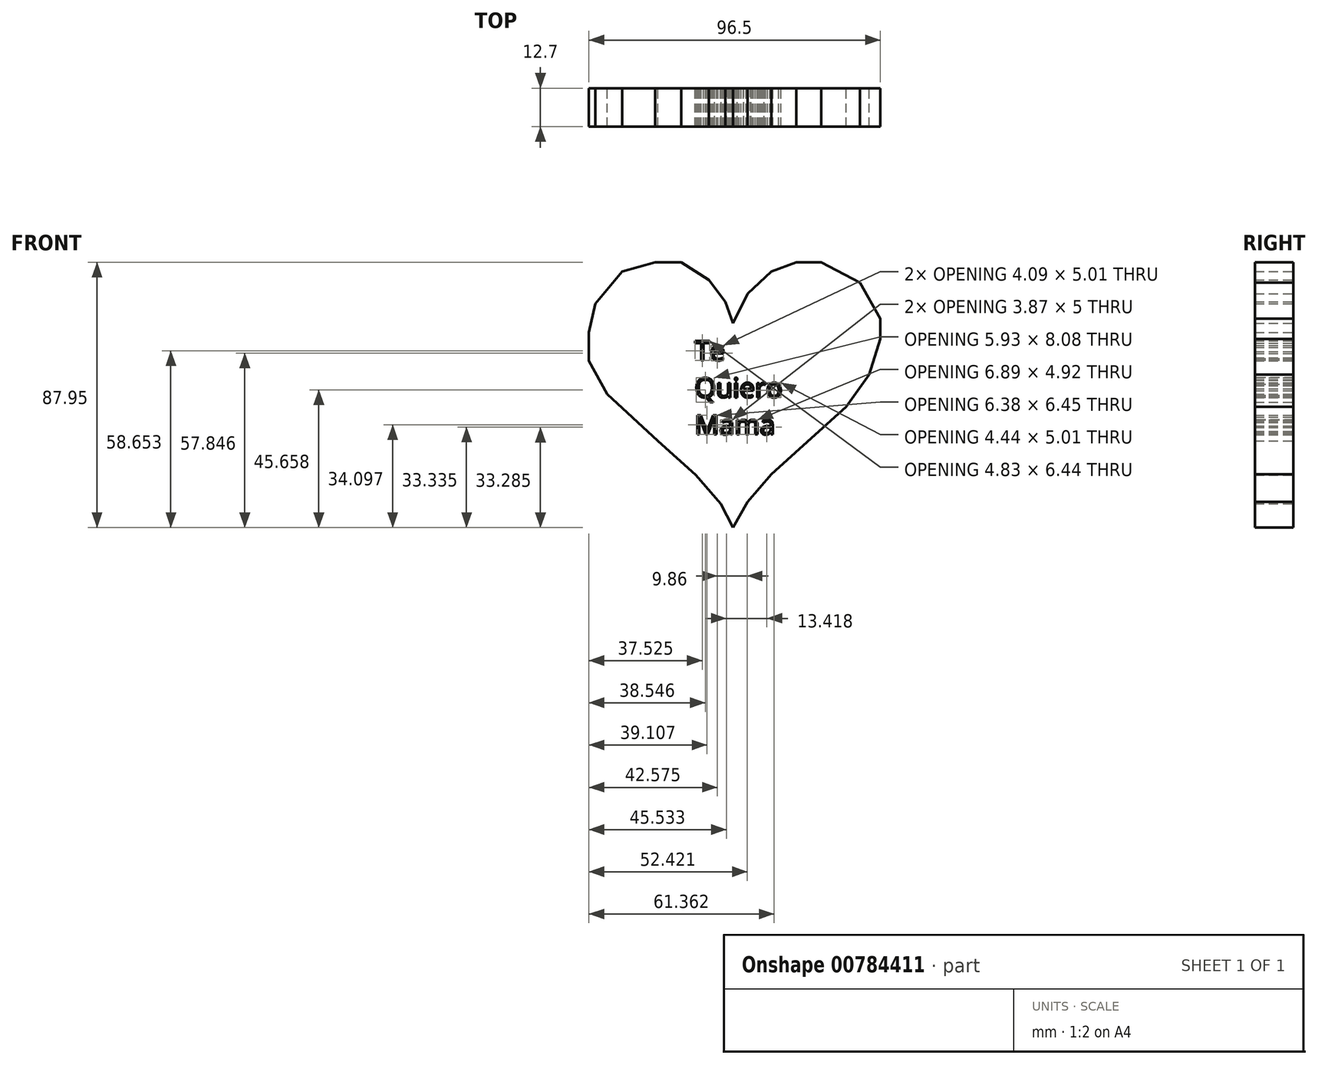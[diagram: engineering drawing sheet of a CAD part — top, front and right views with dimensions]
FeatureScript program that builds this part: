
annotation { "Feature Type Name" : "Feature", "Feature Type Description" : "" }
export const myFeature = defineFeature(function(context is Context, id is Id, definition is map)
    precondition{}
    {
        {
            var Q0;
            Q0=qCreatedBy(makeId("Front.planeOp"),FACE);
            var sketch = newSketch(context, id + "F0", { "sketchPlane" : qUnion([Q0])});
            skLineSegment(sketch, "E0", {"start": v(0, 20.3) * mm, "end": v(4.73, 30.08) * mm});
            skLineSegment(sketch, "E1", {"start": v(4.73, 30.08) * mm, "end": v(12.67, 37.4) * mm});
            skLineSegment(sketch, "E2", {"start": v(12.67, 37.4) * mm, "end": v(20.92, 40.46) * mm});
            skLineSegment(sketch, "E3", {"start": v(20.92, 40.46) * mm, "end": v(29.16, 40.46) * mm});
            skLineSegment(sketch, "E4", {"start": v(29.16, 40.46) * mm, "end": v(41.99, 33.74) * mm});
            skLineSegment(sketch, "E5", {"start": v(41.99, 33.74) * mm, "end": v(48.7, 21.83) * mm});
            skLineSegment(sketch, "E6", {"start": v(48.7, 21.83) * mm, "end": v(48.7, 15.12) * mm});
            skLineSegment(sketch, "E7", {"start": v(48.7, 15.12) * mm, "end": v(45.04, 3.2) * mm});
            skLineSegment(sketch, "E8", {"start": v(45.04, 3.2) * mm, "end": v(37.4, -7.48) * mm});
            skLineSegment(sketch, "E9", {"start": v(37.4, -7.48) * mm, "end": v(25.8, -17.86) * mm});
            skLineSegment(sketch, "E10", {"start": v(25.8, -17.86) * mm, "end": v(12.67, -29.77) * mm});
            skLineSegment(sketch, "E11", {"start": v(12.67, -29.77) * mm, "end": v(4.73, -38.94) * mm});
            skLineSegment(sketch, "E12", {"start": v(4.73, -38.94) * mm, "end": v(0, -47.49) * mm});
            skLineSegment(sketch, "E13", {"start": v(0, -47.49) * mm, "end": v(-4.12, -39.55) * mm});
            skLineSegment(sketch, "E14", {"start": v(-4.12, -39.55) * mm, "end": v(-12.37, -30.08) * mm});
            skLineSegment(sketch, "E15", {"start": v(-12.37, -30.08) * mm, "end": v(-24.89, -18.78) * mm});
            skLineSegment(sketch, "E16", {"start": v(-24.89, -18.78) * mm, "end": v(-41.68, -3.2) * mm});
            skLineSegment(sketch, "E17", {"start": v(-41.68, -3.2) * mm, "end": v(-47.8, 7.79) * mm});
            skLineSegment(sketch, "E18", {"start": v(-47.8, 7.79) * mm, "end": v(-47.8, 17.25) * mm});
            skLineSegment(sketch, "E19", {"start": v(-47.8, 17.25) * mm, "end": v(-45.65, 26.72) * mm});
            skLineSegment(sketch, "E20", {"start": v(-45.65, 26.72) * mm, "end": v(-36.8, 37.4) * mm});
            skLineSegment(sketch, "E21", {"start": v(-36.8, 37.4) * mm, "end": v(-25.8, 40.46) * mm});
            skLineSegment(sketch, "E22", {"start": v(-25.8, 40.46) * mm, "end": v(-17.25, 40.46) * mm});
            skLineSegment(sketch, "E23", {"start": v(-17.25, 40.46) * mm, "end": v(-8.1, 34.66) * mm});
            skLineSegment(sketch, "E24", {"start": v(-8.1, 34.66) * mm, "end": v(-2.6, 27.33) * mm});
            skLineSegment(sketch, "E25", {"start": v(-2.6, 27.33) * mm, "end": v(0, 20.3) * mm});
            skSolve(sketch);
        }
        {
            var Q0;
            Q0=makeQuery(id+"F0.imprint","IMPRINT",FACE,{"disambiguationData":[TD([[makeQuery(id+"F0.imprint","IMPRINT",EDGE,{"derivedFrom":sQuery(id+"F0.wireOp",EDGE,"E0")}),-1.0]])]});
            extrude(context, id + "F1", {"entities" : qUnion([Q0]), "depth" : 12.7 * mm, "offsetDistance" : 25.4 * mm});
        }
        {
            var Q0;
            Q0=qCreatedBy(makeId("Front.planeOp"),FACE);
            var sketch = newSketch(context, id + "F2", { "sketchPlane" : qUnion([Q0])});
            skText(sketch, "E26", { "text": "Te \nQuiero\nMama\n", "fontName": "OpenSans-Regular.ttf"});
            const initialGuessF2  = {"E26": [-0.01276, 0.00794, 1, 0, 0.0065]};
            skSetInitialGuess(sketch, initialGuessF2);
            skSolve(sketch);
        }
        {
            var Q0;
            Q0 = qSketchRegion(id + "F2", true);
            extrude(context, id + "F3", {"entities" : qUnion([Q0]), "operationType" : NewBodyOperationType.REMOVE, "endBound" : BoundingType.THROUGH_ALL, "depth" : 25 * mm, "offsetDistance" : 25 * mm});
        }
    });
